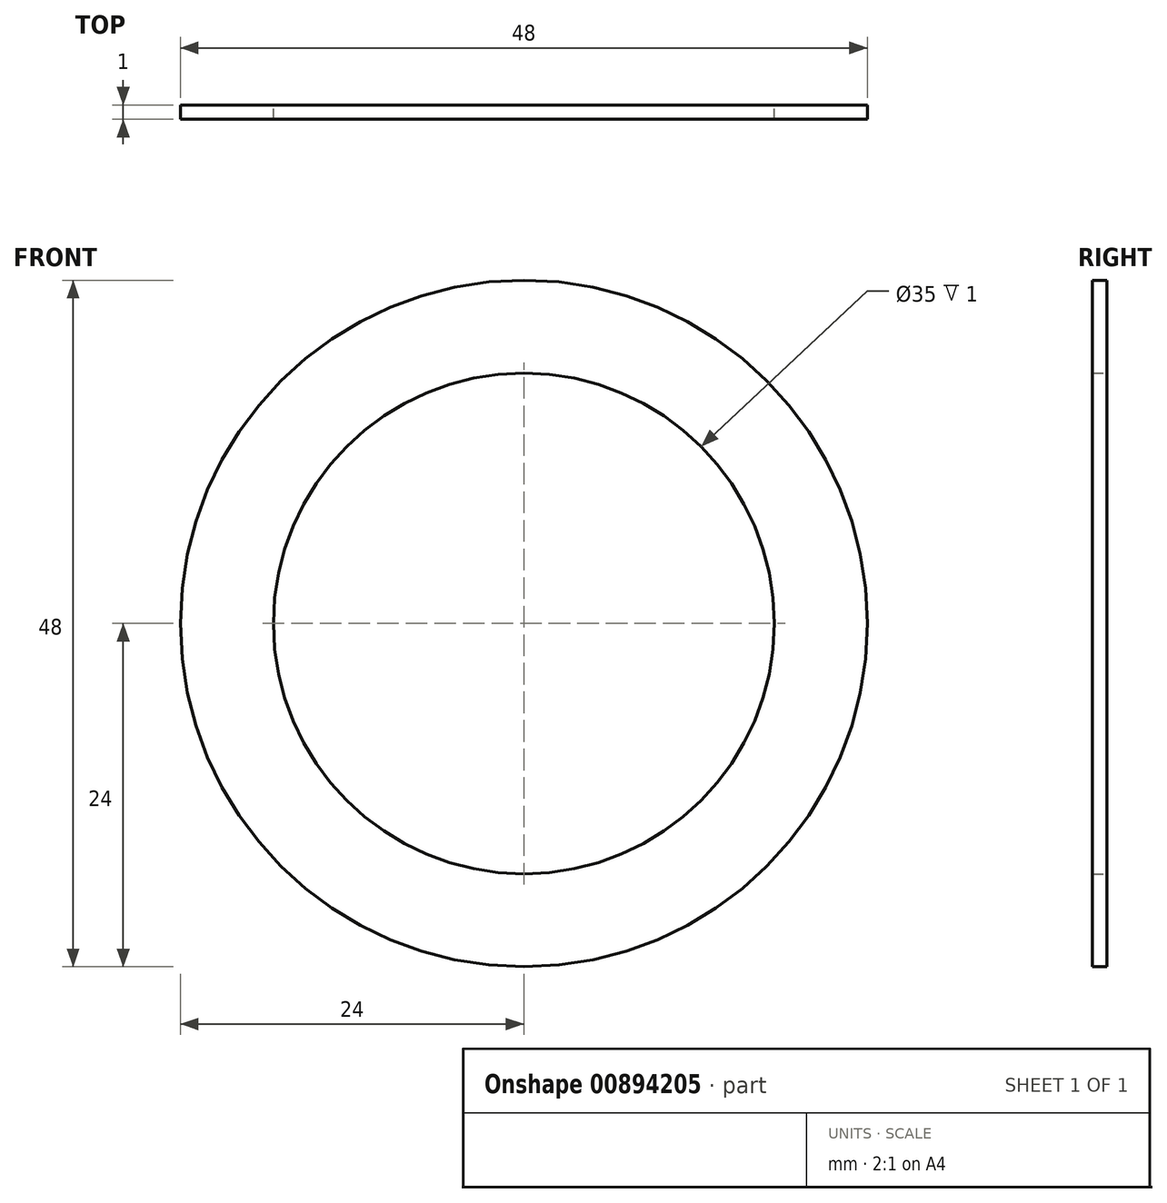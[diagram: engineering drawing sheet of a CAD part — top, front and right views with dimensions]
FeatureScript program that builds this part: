
annotation { "Feature Type Name" : "Feature", "Feature Type Description" : "" }
export const myFeature = defineFeature(function(context is Context, id is Id, definition is map)
    precondition{}
    {
        {
            var Q0;
            Q0=qCreatedBy(makeId("Front.planeOp"),FACE);
            var sketch = newSketch(context, id + "F0", { "sketchPlane" : qUnion([Q0])});
            skCircle(sketch, "E0", {"center": v(0, 0) * mm, "radius": 17.5 * mm});
            skCircle(sketch, "E1", {"center": v(0, 0) * mm, "radius": 24 * mm});
            skSolve(sketch);
        }
        {
            var Q0;
            Q0=makeQuery(id+"F0.imprint","IMPRINT",FACE,{"disambiguationData":[TD([[makeQuery(id+"F0.imprint","IMPRINT",EDGE,{"derivedFrom":sQuery(id+"F0.wireOp",EDGE,"E0")}),-1.0]])]});
            extrude(context, id + "F1", {"entities" : qUnion([Q0]), "depth" : 1 * mm, "offsetDistance" : 25 * mm});
        }
    });
